# Revit family: Table-Teknion-CWRC_Reception_Classic_Desk-R2016
name_source: partatom
category: Furniture
revit_build: Autodesk Revit 2018 (Build: 20190510_1515(x64)
units: mm (PartAtom-declared; Revit-internal decimal feet)

## family parameters
Always vertical = Yes
Cut with Voids When Loaded = No
OmniClass Number = 23.40.20.00
OmniClass Title = General Furniture and Specialties
Room Calculation Point = No
Shared = Yes
Work Plane-Based = No

## types (4) — shared parameters
Assembly Code = E2020200
Depth = 37 "
Manufacturer = Teknion
Manufacturer Fax = 416.661.4586
Part Number = CWRC
Product Documentation Link = https://assets.teknion.com
Product Line = Reception
Product Page URL = https://www.teknion.com
Series = Custom Wood
Sustainability Data = https://www.teknion.com
URL = www.teknion.com
Unit Weight URL = http://www.teknion.com
Warranty = http://www.teknion.com

## per-type parameters (varying)
| type | Description | LB | LF | Left | Model | RB | RF | Right |
| Left, Box/Box/File Storage | Teknion Reception, Classic Desk, 36" Depth, Left, Box/Box/File Storage | Yes | No | Yes | CWRC36_____LB | No | No | No |
| Left, File/File Storage | Teknion Reception, Classic Desk, 36" Depth, Left, File/File Storage | No | Yes | Yes | CWRC36_____LF | No | No | No |
| Right, Box/Box/File Storage | Teknion Reception, Classic Desk, 36" Depth, Right, Box/Box/File Storage | No | No | No | CWRC36_____RB | Yes | No | Yes |
| Right, File/File Storage | Teknion Reception, Classic Desk, 36" Depth, Right, File/File Storage | No | No | No | CWRC36_____RF | No | Yes | Yes |

## geometry (parser evidence)
native form markers: Blend x47, Sweep x2
no freeform markers — native parametric forms only
